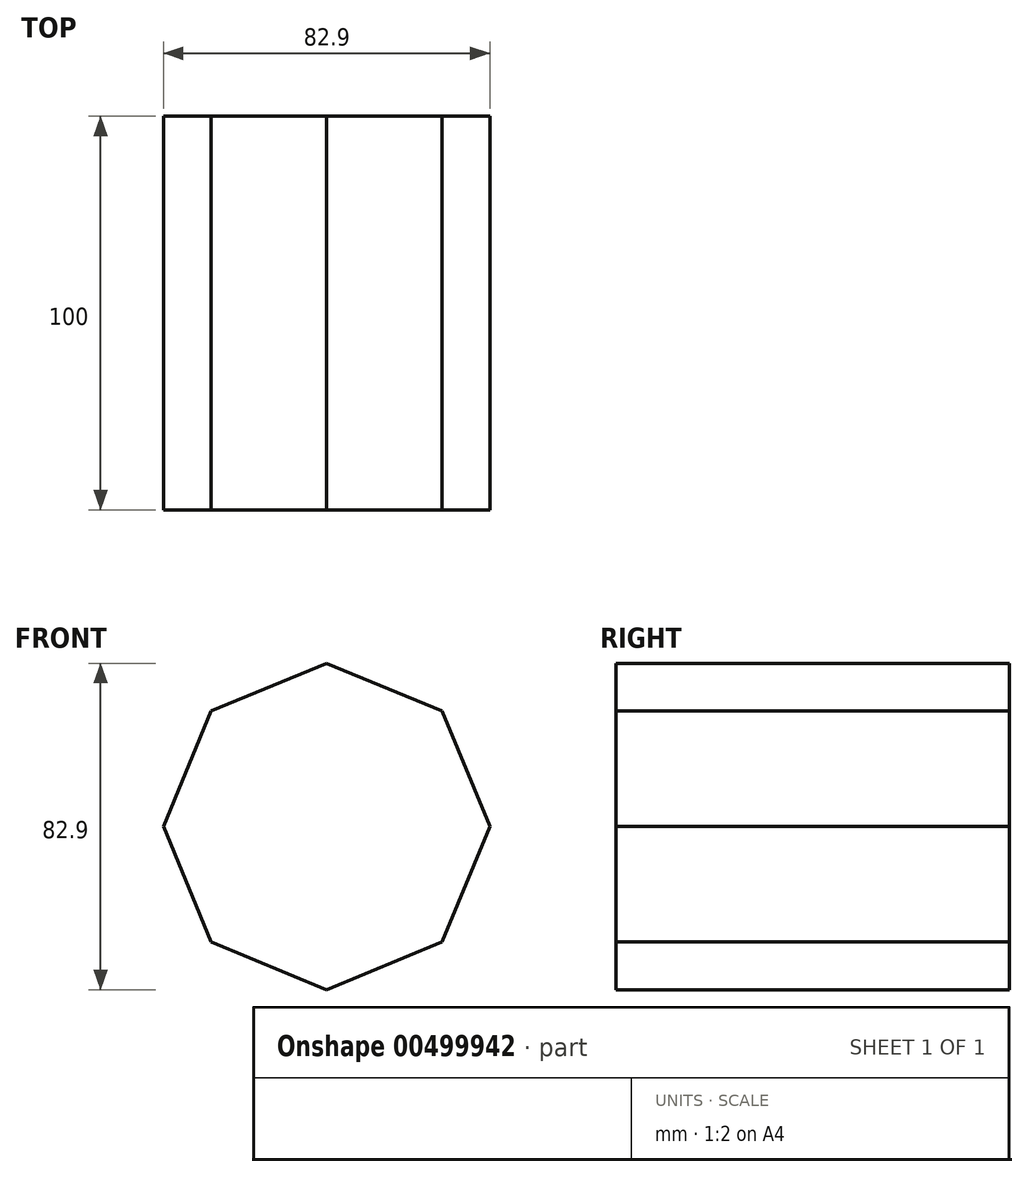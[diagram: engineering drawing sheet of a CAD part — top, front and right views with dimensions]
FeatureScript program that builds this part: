
annotation { "Feature Type Name" : "Feature", "Feature Type Description" : "" }
export const myFeature = defineFeature(function(context is Context, id is Id, definition is map)
    precondition{}
    {
        {
            var Q0;
            Q0=qCreatedBy(makeId("Front.planeOp"),FACE);
            var sketch = newSketch(context, id + "F0", { "sketchPlane" : qUnion([Q0])});
            skCircle(sketch, "E0.cCircle", {"center": v(0, 0) * mm, "radius": 41.45 * mm, "construction": true});
            skLineSegment(sketch, "E0.0", {"start": v(0, 41.45) * mm, "end": v(29.31, 29.31) * mm});
            skLineSegment(sketch, "E0.1", {"start": v(29.31, 29.31) * mm, "end": v(41.45, 0) * mm});
            skLineSegment(sketch, "E0.2", {"start": v(41.45, 0) * mm, "end": v(29.31, -29.31) * mm});
            skLineSegment(sketch, "E0.3", {"start": v(29.31, -29.31) * mm, "end": v(0, -41.45) * mm});
            skLineSegment(sketch, "E0.4", {"start": v(0, -41.45) * mm, "end": v(-29.31, -29.31) * mm});
            skLineSegment(sketch, "E0.5", {"start": v(-29.31, -29.31) * mm, "end": v(-41.45, 0) * mm});
            skLineSegment(sketch, "E0.6", {"start": v(-41.45, 0) * mm, "end": v(-29.31, 29.31) * mm});
            skLineSegment(sketch, "E0.7", {"start": v(-29.31, 29.31) * mm, "end": v(0, 41.45) * mm});
            skSolve(sketch);
        }
        {
            var Q0;
            Q0=makeQuery(id+"F0.imprint","IMPRINT",FACE,{"disambiguationData":[TD([[makeQuery(id+"F0.imprint","IMPRINT",EDGE,{"derivedFrom":sQuery(id+"F0.wireOp",EDGE,"E0.0")}),-1.0]])]});
            extrude(context, id + "F1", {"entities" : qUnion([Q0]), "depth" : 100 * mm});
        }
    });
